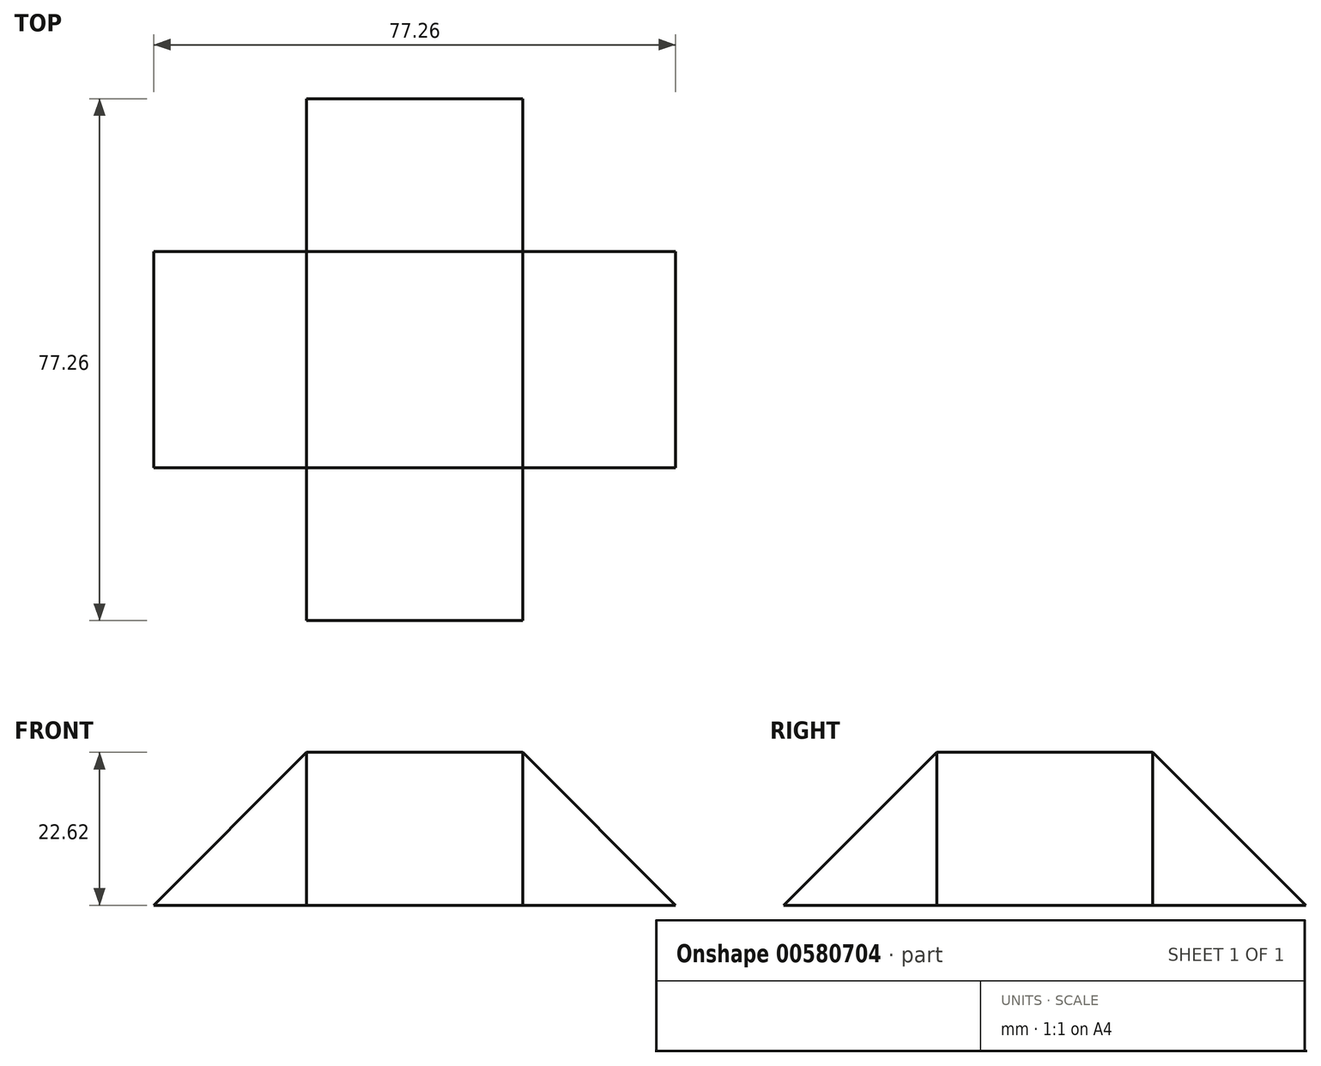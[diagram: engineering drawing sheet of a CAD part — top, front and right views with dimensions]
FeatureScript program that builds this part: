
annotation { "Feature Type Name" : "Feature", "Feature Type Description" : "" }
export const myFeature = defineFeature(function(context is Context, id is Id, definition is map)
    precondition{}
    {
        {
            var Q0;
            Q0=qCreatedBy(makeId("Front.planeOp"),FACE);
            var sketch = newSketch(context, id + "F0", { "sketchPlane" : qUnion([Q0])});
            skLineSegment(sketch, "E0.bottom", {"start": v(-38.63, -11.31) * mm, "end": v(38.63, -11.31) * mm});
            skLineSegment(sketch, "E0.top", {"start": v(-38.63, 11.31) * mm, "end": v(38.63, 11.31) * mm});
            skLineSegment(sketch, "E0.left", {"start": v(-38.63, -11.31) * mm, "end": v(-38.63, 11.31) * mm});
            skLineSegment(sketch, "E0.right", {"start": v(38.63, -11.31) * mm, "end": v(38.63, 11.31) * mm});
            skPoint(sketch, "E0.middle", {"position": v(0, 0) * mm});
            skSolve(sketch);
        }
        {
            var Q0;
            Q0=makeQuery(id+"F0.imprint","IMPRINT",FACE,{"disambiguationData":[TD([[makeQuery(id+"F0.imprint","IMPRINT",EDGE,{"derivedFrom":sQuery(id+"F0.wireOp",EDGE,"E0.bottom")}),1.0]])]});
            extrude(context, id + "F1", {"entities" : qUnion([Q0]), "endBound" : BoundingType.SYMMETRIC, "depth" : 32 * mm, "offsetDistance" : 25 * mm});
        }
        {
            var Q0;
            Q0=makeQuery(id+"F1.opExtrude","SWEPT_EDGE",EDGE,{"disambiguationData":[OSD([sQuery(id+"F0.wireOp",EDGE,"E0.top"),sQuery(id+"F0.wireOp",EDGE,"E0.left")])]});
            var Q1;
            Q1=makeQuery(id+"F1.opExtrude","SWEPT_EDGE",EDGE,{"disambiguationData":[OSD([sQuery(id+"F0.wireOp",EDGE,"E0.top"),sQuery(id+"F0.wireOp",EDGE,"E0.right")])]});
            chamfer(context, id + "F2", {"entities" : qUnion([Q0, Q1]), "width" : 22.63 * mm, "tangentPropagation" : true});
        }
        {
            var Q0;
            Q0=qCreatedBy(makeId("Right.planeOp"),FACE);
            var sketch = newSketch(context, id + "F3", { "sketchPlane" : qUnion([Q0])});
            skLineSegment(sketch, "E1", {"start": v(0, -58.31) * mm, "end": v(0, 53.84) * mm});
            skSolve(sketch);
        }
        {
            var Q0;
            Q0=makeQuery(id+"F1.opExtrude","SWEPT_BODY",BODY,{"disambiguationData":[OSD([sQuery(id+"F0.wireOp",EDGE,"E0.bottom"),sQuery(id+"F0.wireOp",EDGE,"E0.top"),sQuery(id+"F0.wireOp",EDGE,"E0.left"),sQuery(id+"F0.wireOp",EDGE,"E0.right")])]});
            var Q1;
            Q1=sQuery(id+"F3.wireOp",EDGE,"E1");
            circularPattern(context, id + "F4", {"entities" : qUnion([Q0]), "axis" : qUnion([Q1]), "angle" : 90 * degree, "instanceCount" : 2, "equalSpace" : true});
        }
    });
